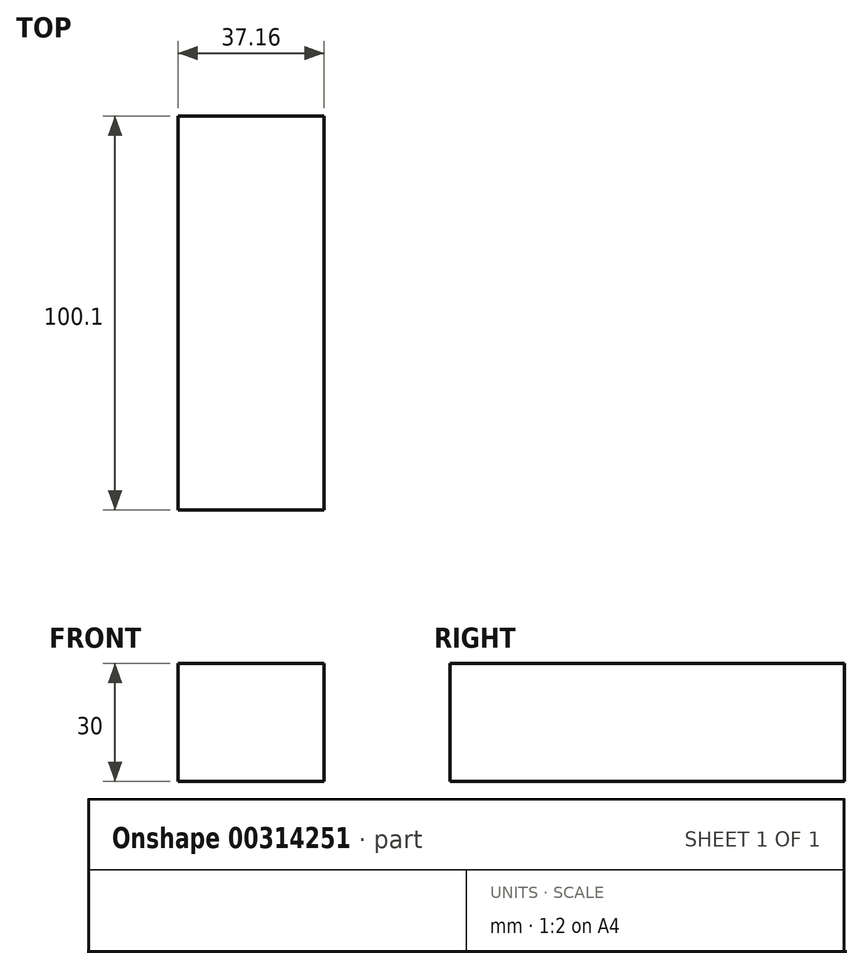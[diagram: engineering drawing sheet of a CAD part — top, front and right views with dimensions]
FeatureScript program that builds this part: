
annotation { "Feature Type Name" : "Feature", "Feature Type Description" : "" }
export const myFeature = defineFeature(function(context is Context, id is Id, definition is map)
    precondition{}
    {
        {
            var Q0;
            Q0=qCreatedBy(makeId("Top.planeOp"),FACE);
            var sketch = newSketch(context, id + "F0", { "sketchPlane" : qUnion([Q0])});
            skLineSegment(sketch, "E0.bottom", {"start": v(-18.58, 50.05) * mm, "end": v(18.58, 50.05) * mm});
            skLineSegment(sketch, "E0.top", {"start": v(-18.58, -50.05) * mm, "end": v(18.58, -50.05) * mm});
            skLineSegment(sketch, "E0.left", {"start": v(-18.58, 50.05) * mm, "end": v(-18.58, -50.05) * mm});
            skLineSegment(sketch, "E0.right", {"start": v(18.58, 50.05) * mm, "end": v(18.58, -50.05) * mm});
            skPoint(sketch, "E0.middle", {"position": v(0, 0) * mm});
            skSolve(sketch);
        }
        {
            var Q0;
            Q0=makeQuery(id+"F0.imprint","IMPRINT",FACE,{"disambiguationData":[TD([[makeQuery(id+"F0.imprint","IMPRINT",EDGE,{"derivedFrom":sQuery(id+"F0.wireOp",EDGE,"E0.bottom")}),-1.0]])]});
            extrude(context, id + "F1", {"entities" : qUnion([Q0]), "depth" : 30 * mm});
        }
    });
